# Revit family: Sink-Top_Under_Mount-Kitchen-KOHLER-Vault-K-3822
name_source: partatom
category: Plumbing Fixtures
revit_build: Autodesk Revit 2015 (Build: 20140606_1530(x64)
units: mm (PartAtom-declared; Revit-internal decimal feet)

## types (3) — shared parameters
ADA Compliant = No
Assembly Code = D2010400
CW Connection = No
Cold Water Inlet = Cold Water Inlet
Date Modified = 4/16/2019
Default Elevation = 36"
Drain Included = No
Finish = Kohler-Metal-NA-Stainless
HW Connection = No
Height = 9 5/16"
Hot Water Inlet = Hot Water Inlet
Length = 25"
Manufacturer = KOHLER Co.
MasterFormat 1995 = 15410
MasterFormat 2004 = 22.41.16
Material = 18-Gauge Stainless Steel
Product Documentation Link = https://www.us.kohler.com
Product Name = Vault
Product Page URL = http://www.us.kohler.com
URL = https://www.us.kohler.com
Vent Connection = No
Waste Connection = Yes
Waste Water Outlet = Waste Water Outlet
WaterSense Certified = No
Width = 22"

## per-type parameters (varying)
| type | Description | Faucet Hole Spacing | Four Faucet Hole | Fourth Hole Spacing | Model | Single Faucet Hole | Three Faucet Hole | Type |
| Single Faucet Hole,NA-Stainless Steel | 25 inch x 22 inch x 9-5/16 inch top-/under-mount medium single-bowl kitchen sink with single faucet hole | 0" | No | 0" | K-3822-1-NA | Yes | No | 1 |
| Three Faucet Hole,NA-Stainless Steel | 25 inch x 22 inch x 9-5/16 inch top-/under-mount medium single-bowl kitchen sink with 3 faucet holes | 8" | No | 0" | K-3822-3-NA | No | Yes | 2 |
| Four Faucet Hole,NA-Stainless Steel | 25 inch x 22 inch x 9-5/16 inch top-/under-mount medium single-bowl kitchen sink with 4 faucet holes | 8" | Yes | 9 1/2" | K-3822-4-NA | No | No | 3 |

## geometry (parser evidence)
native form markers: Sweep x5
no freeform markers — native parametric forms only
